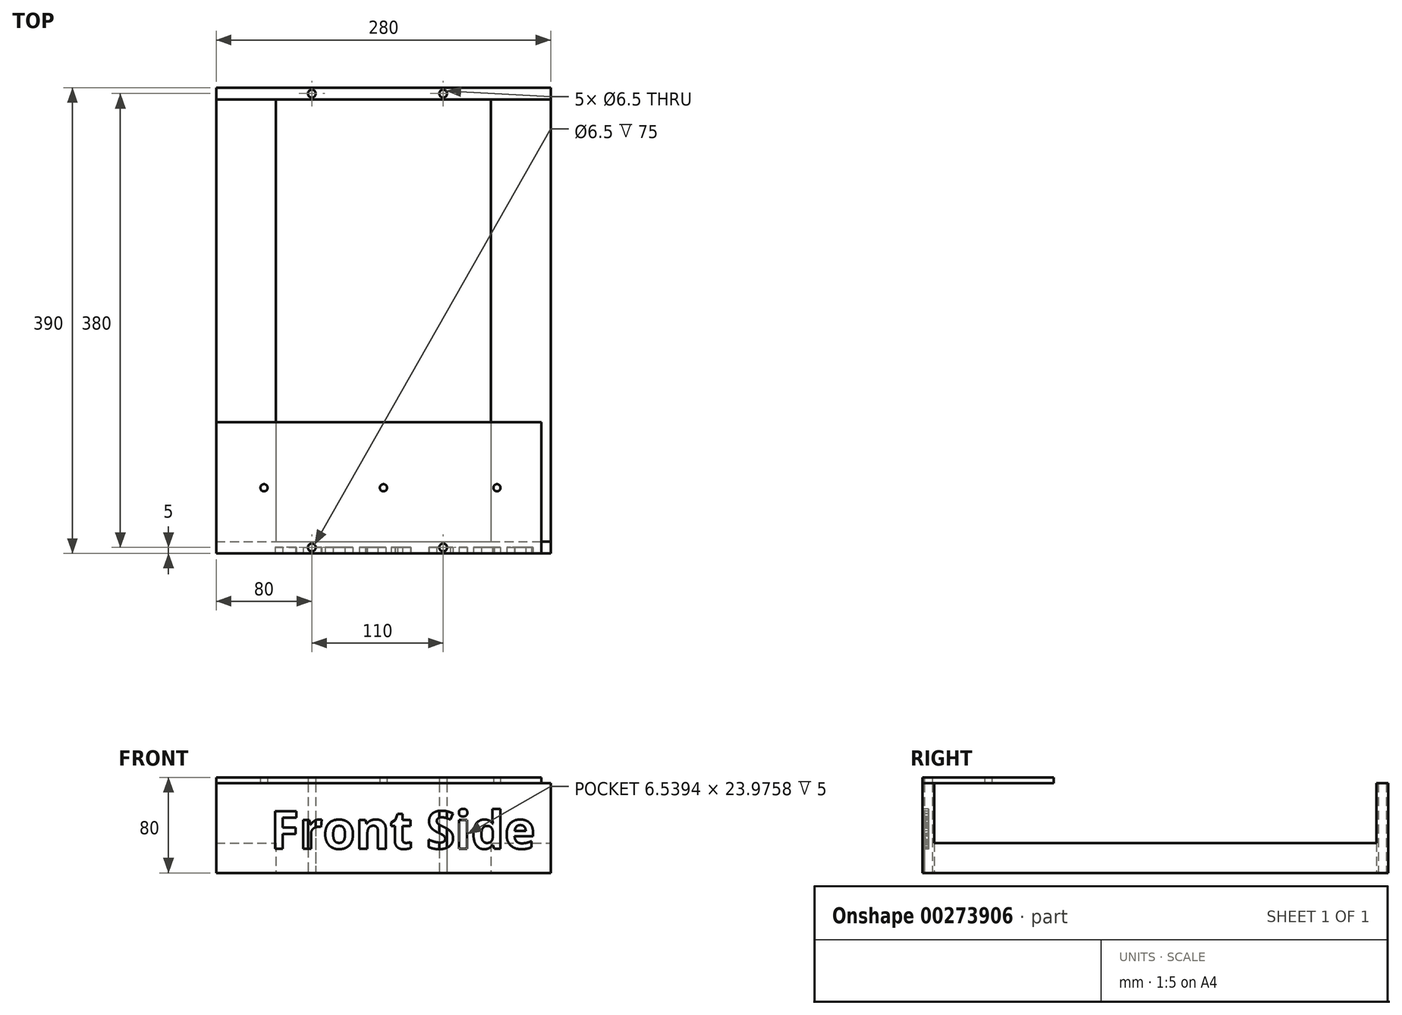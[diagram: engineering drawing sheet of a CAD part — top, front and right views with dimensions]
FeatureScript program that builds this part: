
annotation { "Feature Type Name" : "Feature", "Feature Type Description" : "" }
export const myFeature = defineFeature(function(context is Context, id is Id, definition is map)
    precondition{}
    {
        {
            var Q0;
            Q0=qCreatedBy(makeId("Top.planeOp"),FACE);
            var sketch = newSketch(context, id + "F0", { "sketchPlane" : qUnion([Q0])});
            skLineSegment(sketch, "E0.bottom", {"start": v(0, 0) * mm, "end": v(-280, 0) * mm});
            skLineSegment(sketch, "E0.top", {"start": v(0, 390) * mm, "end": v(-280, 390) * mm});
            skLineSegment(sketch, "E0.left", {"start": v(0, 0) * mm, "end": v(0, 390) * mm});
            skLineSegment(sketch, "E0.right", {"start": v(-280, 0) * mm, "end": v(-280, 390) * mm});
            skLineSegment(sketch, "E1", {"start": v(-280, 195) * mm, "end": v(0, 195) * mm, "construction": true});
            skCircle(sketch, "E2", {"center": v(-200, 5) * mm, "radius": 3.25 * mm});
            skCircle(sketch, "E3", {"center": v(-90, 5) * mm, "radius": 3.25 * mm});
            skLineSegment(sketch, "E4", {"start": v(-280, 10) * mm, "end": v(0, 10) * mm});
            skLineSegment(sketch, "E5.MirrorCS", {"start": v(-280, 380) * mm, "end": v(0, 380) * mm});
            skCircle(sketch, "E6.MirrorC", {"center": v(-200, 385) * mm, "radius": 3.25 * mm});
            skCircle(sketch, "E7.MirrorC", {"center": v(-90, 385) * mm, "radius": 3.25 * mm});
            skLineSegment(sketch, "E8", {"start": v(-230, 380) * mm, "end": v(-230, 10) * mm});
            skLineSegment(sketch, "E9", {"start": v(-50, 380) * mm, "end": v(-50, 10) * mm});
            skLineSegment(sketch, "E10.bottom", {"start": v(-280, 0) * mm, "end": v(-8, 0) * mm});
            skLineSegment(sketch, "E10.top", {"start": v(-280, 110) * mm, "end": v(-8, 110) * mm});
            skLineSegment(sketch, "E10.left", {"start": v(-280, 0) * mm, "end": v(-280, 110) * mm});
            skLineSegment(sketch, "E10.right", {"start": v(-8, 0) * mm, "end": v(-8, 110) * mm});
            skCircle(sketch, "E11", {"center": v(-140, 55) * mm, "radius": 3 * mm});
            skCircle(sketch, "E12", {"center": v(-45, 55) * mm, "radius": 3 * mm});
            skCircle(sketch, "E13", {"center": v(-240, 55) * mm, "radius": 3 * mm});
            skSolve(sketch);
        }
        {
            var Q0;
            {var subQ1=sQuery(id+"F0.wireOp",EDGE,"E0.bottom");Q0=makeQuery(id+"F0.imprint","IMPRINT",FACE,{"disambiguationData":[TD([[makeQuery(id+"F0.imprint","IMPRINT",EDGE,{"derivedFrom":subQ1}),-1.0]])]});}
            var Q1;
            {var subQ4=sQuery(id+"F0.wireOp",EDGE,"E0.top");Q1=makeQuery(id+"F0.imprint","IMPRINT",FACE,{"disambiguationData":[TD([[makeQuery(id+"F0.imprint","IMPRINT",EDGE,{"derivedFrom":subQ4}),1.0]])]});}
            var Q2;
            Q2=makeQuery(id+"F0.imprint","IMPRINT",FACE,{"disambiguationData":[TD([[makeQuery(id+"F0.imprint","IMPRINT",EDGE,{"derivedFrom":sQuery(id+"F0.wireOp",EDGE,"E2")}),-1.0]])]});
            extrude(context, id + "F1", {"entities" : qUnion([Q0, Q1, Q2]), "depth" : 75 * mm});
        }
        {
            var Q0;
            {var subQ5=sQuery(id+"F0.wireOp",EDGE,"E8");Q0=makeQuery(id+"F0.imprint","IMPRINT",FACE,{"disambiguationData":[TD([[makeQuery(id+"F0.imprint","IMPRINT",EDGE,{"derivedFrom":subQ5}),-1.0]])]});}
            var Q1;
            {var subQ5=sQuery(id+"F0.wireOp",EDGE,"E9");Q1=makeQuery(id+"F0.imprint","IMPRINT",FACE,{"disambiguationData":[TD([[makeQuery(id+"F0.imprint","IMPRINT",EDGE,{"derivedFrom":subQ5}),1.0]])]});}
            var Q2;
            Q2=makeQuery(id+"F0.imprint","IMPRINT",FACE,{"disambiguationData":[TD([[makeQuery(id+"F0.imprint","IMPRINT",EDGE,{"derivedFrom":sQuery(id+"F0.wireOp",EDGE,"E13")}),-1.0]])]});
            var Q3;
            Q3=makeQuery(id+"F0.imprint","IMPRINT",FACE,{"disambiguationData":[TD([[makeQuery(id+"F0.imprint","IMPRINT",EDGE,{"derivedFrom":sQuery(id+"F0.wireOp",EDGE,"E12")}),-1.0]])]});
            var Q4;
            Q4=makeQuery(id+"F0.imprint","IMPRINT",FACE,{"disambiguationData":[TD([[makeQuery(id+"F0.imprint","IMPRINT",EDGE,{"derivedFrom":sQuery(id+"F0.wireOp",EDGE,"E13")}),1.0]])]});
            var Q5;
            Q5=makeQuery(id+"F0.imprint","IMPRINT",FACE,{"disambiguationData":[TD([[makeQuery(id+"F0.imprint","IMPRINT",EDGE,{"derivedFrom":sQuery(id+"F0.wireOp",EDGE,"E12")}),1.0]])]});
            var Q6;
            {var subQ5=sQuery(id+"F0.wireOp",EDGE,"E0.left");var subQ7=sQuery(id+"F0.wireOp",EDGE,"E4");var subQ8=makeQuery(id+"F0.imprint","INTERSECT",VERTEX,{"derivedFrom":[subQ5,subQ7]});Q6=makeQuery(id+"F0.imprint","IMPRINT",FACE,{"disambiguationData":[TD([[makeQuery(id+"F0.imprint","IMPRINT",EDGE,{"disambiguationData":[TD([[subQ8,-1.0]])],"derivedFrom":subQ5}),1.0]])]});}
            extrude(context, id + "F2", {"entities" : qUnion([Q0, Q1, Q2, Q3, Q4, Q5, Q6]), "operationType" : NewBodyOperationType.ADD, "depth" : 25 * mm});
        }
        {
            var Q0;
            Q0=makeQuery(id+"F1.opExtrude","SWEPT_FACE",FACE,{"disambiguationData":[OSD([sQuery(id+"F0.wireOp",EDGE,"E0.bottom")])]});
            var sketch = newSketch(context, id + "F3", { "sketchPlane" : qUnion([Q0])});
            skText(sketch, "E14", { "text": "Front Side", "fontName": "OpenSans-Bold.ttf"});
            const initialGuessF3  = {"E14": [-0.2348, 0.02028, 1, 0, 0.03162]};
            skSetInitialGuess(sketch, initialGuessF3);
            skSolve(sketch);
        }
        {
            var Q0;
            Q0 = qSketchRegion(id + "F3", true);
            extrude(context, id + "F4", {"entities" : qUnion([Q0]), "operationType" : NewBodyOperationType.REMOVE, "oppositeDirection" : true, "depth" : 5 * mm});
        }
        {
            var Q0;
            Q0=makeQuery(id+"F0.imprint","IMPRINT",FACE,{"disambiguationData":[TD([[makeQuery(id+"F0.imprint","IMPRINT",EDGE,{"derivedFrom":sQuery(id+"F0.wireOp",EDGE,"E13")}),-1.0]])]});
            var Q1;
            Q1=makeQuery(id+"F0.imprint","IMPRINT",FACE,{"disambiguationData":[TD([[makeQuery(id+"F0.imprint","IMPRINT",EDGE,{"derivedFrom":sQuery(id+"F0.wireOp",EDGE,"E11")}),-1.0]])]});
            var Q2;
            {var subQ0=sQuery(id+"F0.wireOp",EDGE,"E9");var subQ1=sQuery(id+"F0.wireOp",EDGE,"E4");var subQ2=makeQuery(id+"F0.imprint","INTERSECT",VERTEX,{"derivedFrom":[subQ1,subQ0]});Q2=makeQuery(id+"F0.imprint","IMPRINT",FACE,{"disambiguationData":[TD([[makeQuery(id+"F0.imprint","IMPRINT",EDGE,{"disambiguationData":[TD([[subQ2,-1.0]])],"derivedFrom":subQ1}),1.0]])]});}
            var Q3;
            Q3=makeQuery(id+"F0.imprint","IMPRINT",FACE,{"disambiguationData":[TD([[makeQuery(id+"F0.imprint","IMPRINT",EDGE,{"derivedFrom":sQuery(id+"F0.wireOp",EDGE,"E2")}),-1.0]])]});
            extrude(context, id + "F5", {"entities" : qUnion([Q0, Q1, Q2, Q3]), "depth" : 80 * mm, "hasSecondDirection" : true, "secondDirectionOppositeDirection" : false, "secondDirectionDepth" : 75 * mm});
        }
    });
